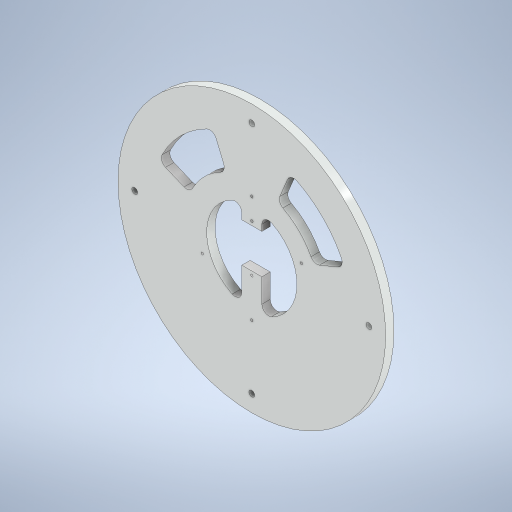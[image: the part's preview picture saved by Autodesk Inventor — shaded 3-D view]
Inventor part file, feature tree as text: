
AUTODESK INVENTOR PART (.ipt)
format: ipt  version: 2023 (Build 270158000, 158)  size: 333,824 bytes
history: native  units: mm
features: extrude x5, sketch x4, fillet x2, other x1, pattern_circular x1, mirror x1
ambient origin geometry x8: Origin, YZ Plane, XZ Plane, XY Plane, X Axis, Y Axis, Z Axis, Center Point
bodies: Body1 (feature_tree)
feature tree (14):
  other  "솔리드1"
  sketch  "스케치1"
  extrude  "돌출1"  Depth=160.0mm
  extrude  "돌출2"  Depth=68.0mm
  fillet  "모깎기1"  Radius=54.0mm
  extrude  "돌출3"  Depth=120.0mm
  pattern_circular  "원형 패턴2"  Count=8  [1 undecoded]
  extrude  "돌출4"  TaperAngle=45.0deg  [1 undecoded]
  fillet  "모깎기2"  Radius=5.0mm
  extrude  "돌출5"  Depth=5.0mm TaperAngle=0.0deg
  mirror  "미러1"
  sketch  "스케치2"
  sketch  "스케치3"
  sketch  "스케치4"
note: 2 required parameter values undecoded (feature->parameter linkage not recoverable at this tier; creation-order binding heuristic only, values carry confidence <= 0.55)
